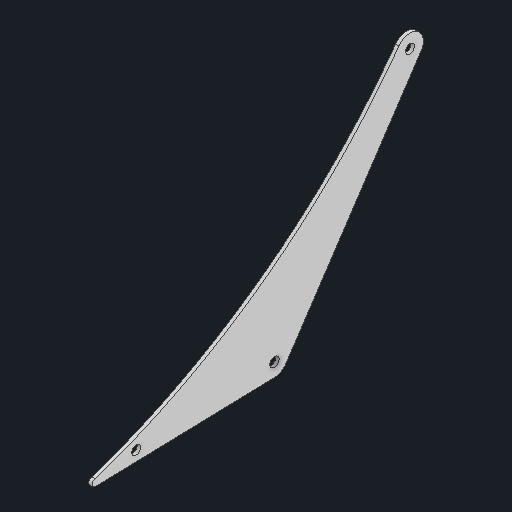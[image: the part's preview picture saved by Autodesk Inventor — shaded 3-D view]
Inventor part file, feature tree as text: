
AUTODESK INVENTOR PART (.ipt)
format: ipt  version: 2025 (Build 290162000, 162)  size: 98,816 bytes
history: native  units: in
note: dims shown in document units (in); Inventor stores cm internally (conversion verified against a paired STEP export)
features: other x3, extrude x1, sketch x1
ambient origin geometry x8: Origin, YZ Plane, XZ Plane, XY Plane, X Axis, Y Axis, Z Axis, Center Point
bodies: Solid1 (feature_tree)
feature tree (5):
  other  "Blocks"
  extrude  "Extrusion1"  Depth=0.0625in
  sketch  "Sketch1"  dims[d3=0.0625in d4=0.0in d5=0.5in d6=0.164in]
  other  "main"
  other  "main:1"
